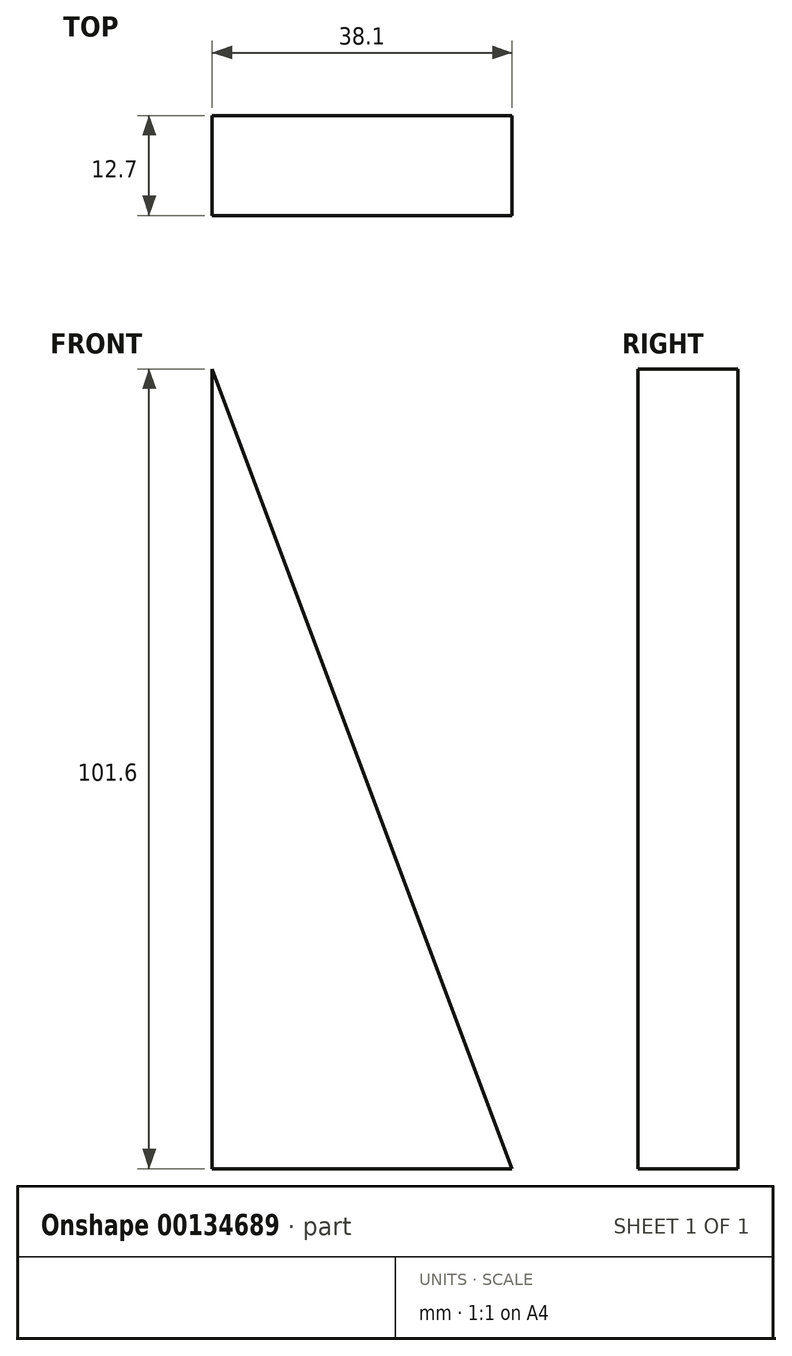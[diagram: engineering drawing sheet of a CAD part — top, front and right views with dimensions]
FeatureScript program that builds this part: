
annotation { "Feature Type Name" : "Feature", "Feature Type Description" : "" }
export const myFeature = defineFeature(function(context is Context, id is Id, definition is map)
    precondition{}
    {
        {
            var Q0;
            Q0=qCreatedBy(makeId("Front.planeOp"),FACE);
            var sketch = newSketch(context, id + "F0", { "sketchPlane" : qUnion([Q0])});
            skLineSegment(sketch, "E0", {"start": v(-37.9, 52.38) * mm, "end": v(-37.9, -49.22) * mm});
            skLineSegment(sketch, "E1", {"start": v(-37.9, -49.22) * mm, "end": v(0.2, -49.22) * mm});
            skLineSegment(sketch, "E2", {"start": v(0.2, -49.22) * mm, "end": v(-37.9, 52.38) * mm});
            skSolve(sketch);
        }
        {
            var Q0;
            Q0 = qSketchRegion(id + "F0", true);
            extrude(context, id + "F1", {"entities" : qUnion([Q0]), "depth" : 12.7 * mm});
        }
    });
